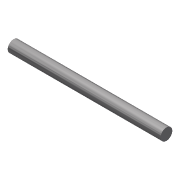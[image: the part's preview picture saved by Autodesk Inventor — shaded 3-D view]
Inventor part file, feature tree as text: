
AUTODESK INVENTOR PART (.ipt)
format: ipt  version: 2016 (Build 200138000, 138)  size: 70,144 bytes
history: native  units: in
note: dims shown in document units (in); Inventor stores cm internally (conversion verified against a paired STEP export)
features: extrude x1, sketch x1
ambient origin geometry x8: Origin, YZ Plane, XZ Plane, XY Plane, X Axis, Y Axis, Z Axis, Center Point
bodies: Solid1 (feature_tree)
feature tree (2):
  extrude  "Extrusion1"  Depth=4.875in TaperAngle=0.0deg
  sketch  "Sketch1"  dims[d0=0.375in d1=4.875in d2=0.0in]
